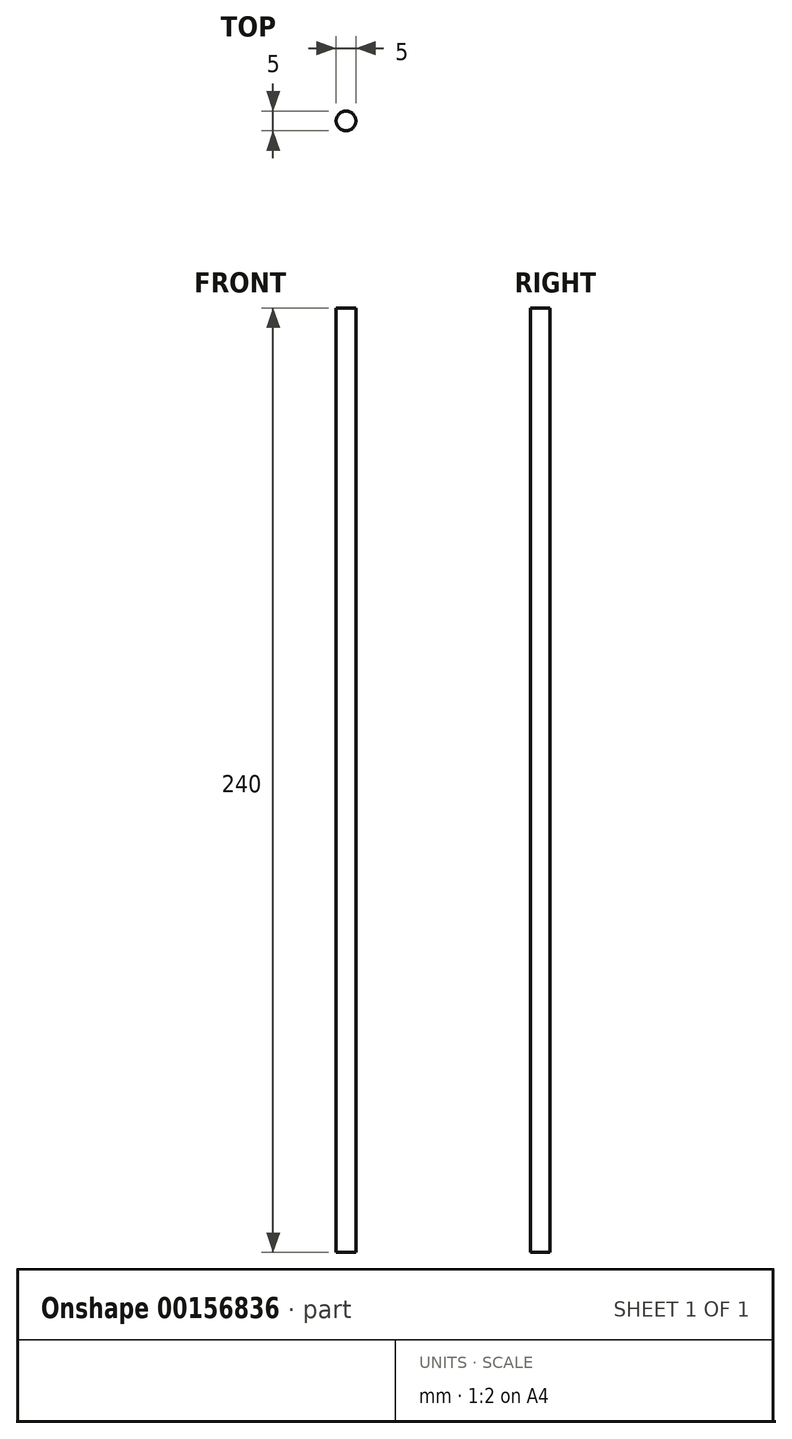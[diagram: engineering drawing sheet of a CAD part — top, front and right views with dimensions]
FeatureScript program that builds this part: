
annotation { "Feature Type Name" : "Feature", "Feature Type Description" : "" }
export const myFeature = defineFeature(function(context is Context, id is Id, definition is map)
    precondition{}
    {
        {
            var Q0;
            Q0=qCreatedBy(makeId("Top.planeOp"),FACE);
            var sketch = newSketch(context, id + "F0", { "sketchPlane" : qUnion([Q0])});
            skCircle(sketch, "E0", {"center": v(0, 0) * mm, "radius": 2.5 * mm});
            skSolve(sketch);
        }
        {
            var Q0;
            Q0=qSketchRegion(id+"F0",true);
            extrude(context, id + "F1", {"entities" : qUnion([Q0]), "endBound" : BoundingType.SYMMETRIC, "depth" : 240 * mm});
        }
    });
